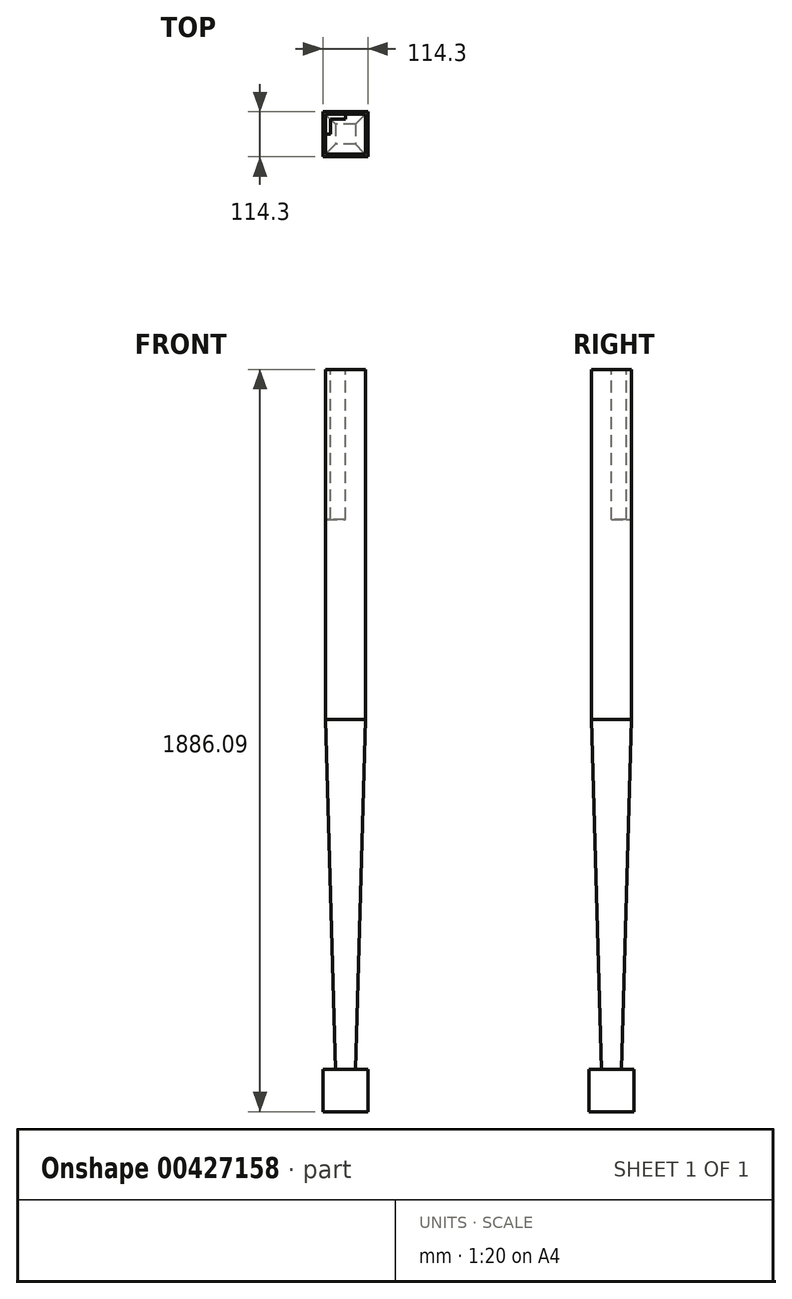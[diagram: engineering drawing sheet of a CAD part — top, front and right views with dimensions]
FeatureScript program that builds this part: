
annotation { "Feature Type Name" : "Feature", "Feature Type Description" : "" }
export const myFeature = defineFeature(function(context is Context, id is Id, definition is map)
    precondition{}
    {
        {
            var Q0;
            Q0=qCreatedBy(makeId("Front.planeOp"),FACE);
            var sketch = newSketch(context, id + "F0", { "sketchPlane" : qUnion([Q0])});
            skLineSegment(sketch, "E0.bottom", {"start": v(-493.32, 889) * mm, "end": v(-391.72, 889) * mm});
            skLineSegment(sketch, "E0.top", {"start": v(-493.32, 0) * mm, "end": v(-391.72, 0) * mm});
            skLineSegment(sketch, "E0.left", {"start": v(-493.32, 889) * mm, "end": v(-493.32, 0) * mm});
            skLineSegment(sketch, "E0.right", {"start": v(-391.72, 889) * mm, "end": v(-391.72, 0) * mm});
            skLineSegment(sketch, "E1.bottom", {"start": v(-467.92, 0) * mm, "end": v(-417.12, 0) * mm});
            skLineSegment(sketch, "E1.top", {"start": v(-467.92, -889) * mm, "end": v(-417.12, -889) * mm});
            skLineSegment(sketch, "E1.left", {"start": v(-467.92, 0) * mm, "end": v(-467.92, -889) * mm});
            skLineSegment(sketch, "E1.right", {"start": v(-417.12, 0) * mm, "end": v(-417.12, -889) * mm});
            skLineSegment(sketch, "E2", {"start": v(-493.32, 0) * mm, "end": v(-467.92, -889) * mm});
            skLineSegment(sketch, "E3", {"start": v(-417.12, -889) * mm, "end": v(-391.72, 0) * mm});
            skLineSegment(sketch, "E4.bottom", {"start": v(-499.67, -889) * mm, "end": v(-385.37, -889) * mm});
            skLineSegment(sketch, "E4.top", {"start": v(-499.67, -997.09) * mm, "end": v(-385.37, -997.09) * mm});
            skLineSegment(sketch, "E4.left", {"start": v(-499.67, -889) * mm, "end": v(-499.67, -997.09) * mm});
            skLineSegment(sketch, "E4.right", {"start": v(-385.37, -889) * mm, "end": v(-385.37, -997.09) * mm});
            skSolve(sketch);
        }
        {
            var Q0;
            Q0=makeQuery(id+"F0.imprint","IMPRINT",FACE,{"disambiguationData":[TD([[makeQuery(id+"F0.imprint","IMPRINT",EDGE,{"derivedFrom":sQuery(id+"F0.wireOp",EDGE,"E4.top")}),1.0]])]});
            extrude(context, id + "F1", {"entities" : qUnion([Q0]), "endBound" : BoundingType.SYMMETRIC, "depth" : 114.3 * mm, "offsetDistance" : 25.4 * mm});
        }
        {
            var Q0;
            Q0=makeQuery(id+"F0.imprint","IMPRINT",FACE,{"disambiguationData":[TD([[makeQuery(id+"F0.imprint","IMPRINT",EDGE,{"derivedFrom":sQuery(id+"F0.wireOp",EDGE,"E0.bottom")}),-1.0]])]});
            extrude(context, id + "F2", {"entities" : qUnion([Q0]), "endBound" : BoundingType.SYMMETRIC, "depth" : 101.6 * mm, "offsetDistance" : 25.4 * mm});
        }
        {
            var Q0;
            Q0=makeQuery(id+"F1.opExtrude","SWEPT_FACE",FACE,{"disambiguationData":[OSD([sQuery(id+"F0.wireOp",EDGE,"E4.bottom")])]});
            var sketch = newSketch(context, id + "F3", { "sketchPlane" : qUnion([Q0])});
            skLineSegment(sketch, "E5.bottom", {"start": v(-417.12, 25.4) * mm, "end": v(-467.92, 25.4) * mm});
            skLineSegment(sketch, "E5.top", {"start": v(-417.12, -25.4) * mm, "end": v(-467.92, -25.4) * mm});
            skLineSegment(sketch, "E5.left", {"start": v(-417.12, 25.4) * mm, "end": v(-417.12, -25.4) * mm});
            skLineSegment(sketch, "E5.right", {"start": v(-467.92, 25.4) * mm, "end": v(-467.92, -25.4) * mm});
            skPoint(sketch, "E5.middle", {"position": v(-442.52, 0) * mm});
            skPoint(sketch, "E5.middle.positionSnap0", {"position": v(-499.67, 0) * mm});
            skPoint(sketch, "E5.middle.positionSnap1", {"position": v(-442.52, 57.15) * mm});
            skPoint(sketch, "E5.centerSnap0", {"position": v(-499.67, 0) * mm});
            skPoint(sketch, "E5.centerSnap1", {"position": v(-442.52, 57.15) * mm});
            skSolve(sketch);
        }
        {
            var Q0;
            Q0=makeQuery(id+"F3.imprint","IMPRINT",FACE,{"disambiguationData":[TD([[makeQuery(id+"F3.imprint","IMPRINT",EDGE,{"derivedFrom":sQuery(id+"F3.wireOp",EDGE,"E5.bottom")}),1.0]])]});
            var Q1;
            Q1=makeQuery(id+"F2.opExtrude","SWEPT_FACE",FACE,{"disambiguationData":[OSD([sQuery(id+"F0.wireOp",EDGE,"E0.top"),sQuery(id+"F0.wireOp",EDGE,"E1.bottom")])]});
            loft(context, id + "F4", {"sheetProfilesArray" : [{ "sheetProfileEntities" : qUnion([Q0]) }, { "sheetProfileEntities" : qUnion([Q1]) }]});
        }
        {
            var Q0;
            Q0=makeQuery(id+"F2.opExtrude","SWEPT_FACE",FACE,{"disambiguationData":[OSD([sQuery(id+"F0.wireOp",EDGE,"E0.bottom")])]});
            var sketch = newSketch(context, id + "F5", { "sketchPlane" : qUnion([Q0])});
            skLineSegment(sketch, "E6.bottom", {"start": v(-404.42, 38.1) * mm, "end": v(-480.62, 38.1) * mm});
            skLineSegment(sketch, "E6.top", {"start": v(-404.42, -38.1) * mm, "end": v(-480.62, -38.1) * mm});
            skLineSegment(sketch, "E6.left", {"start": v(-404.42, 38.1) * mm, "end": v(-404.42, -38.1) * mm});
            skLineSegment(sketch, "E6.right", {"start": v(-480.62, 38.1) * mm, "end": v(-480.62, -38.1) * mm});
            skPoint(sketch, "E6.middle", {"position": v(-442.52, 0) * mm});
            skPoint(sketch, "E6.middle.positionSnap0", {"position": v(-442.52, 50.8) * mm});
            skPoint(sketch, "E6.centerSnap0", {"position": v(-442.52, 50.8) * mm});
            skLineSegment(sketch, "E7", {"start": v(-442.52, 38.1) * mm, "end": v(-442.52, 50.8) * mm});
            skLineSegment(sketch, "E8", {"start": v(-480.62, 0) * mm, "end": v(-493.32, 0) * mm});
            skSolve(sketch);
        }
        {
            var Q0;
            {var subQ4=sQuery(id+"F5.wireOp",EDGE,"E7");Q0=makeQuery(id+"F5.imprint","IMPRINT",FACE,{"disambiguationData":[TD([[makeQuery(id+"F5.imprint","IMPRINT",EDGE,{"derivedFrom":subQ4}),1.0]])]});}
            extrude(context, id + "F6", {"entities" : qUnion([Q0]), "operationType" : NewBodyOperationType.REMOVE, "oppositeDirection" : true, "depth" : 381 * mm, "offsetDistance" : 25.4 * mm});
        }
    });
